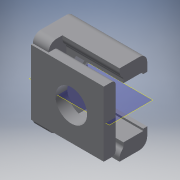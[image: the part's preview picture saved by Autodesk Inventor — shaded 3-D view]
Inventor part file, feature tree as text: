
AUTODESK INVENTOR PART (.ipt)
format: ipt  version: 2016 (Build 200138000, 138)  size: 312,320 bytes
history: native  units: mm
features: extrude x14, sketch x14, projected_geometry x7, fillet x3, plane x1, mirror x1, move_body x1
ambient origin geometry x8: Origin, YZ Plane, XZ Plane, XY Plane, X Axis, Y Axis, Z Axis, Center Point
bodies: Solid1 (feature_tree)
feature tree (41):
  extrude  "Extrusion1"  Depth=16.5mm
  sketch  "Sketch2"  dims[d2=11.0mm d3=0.0mm d4=6.0mm]
  extrude  "Extrusion2"  Depth=6.0mm
  extrude  "Extrusion3"  Depth=2.0mm
  extrude  "Extrusion4"  Depth=13.0mm
  extrude  "Extrusion5"  Depth=8.0mm
  extrude  "Extrusion6"  Depth=12.5mm TaperAngle=0.0deg
  extrude  "Extrusion7"  Depth=12.5mm TaperAngle=0.0deg
  extrude  "Extrusion8"  Depth=1.0mm TaperAngle=0.0deg
  extrude  "Extrusion9"  Depth=16.5mm
  extrude  "Extrusion10"  Depth=1.0mm
  plane  "Work Plane1"
  mirror  "Mirror1"
  extrude  "Extrusion11"  Depth=2.0mm TaperAngle=0.0deg
  fillet  "Fillet3"  Radius=2.0mm
  fillet  "Fillet4"  Radius=2.0mm
  fillet  "Fillet5"  Radius=2.0mm
  extrude  "Extrusion12"  Depth=2.0mm TaperAngle=0.0deg
  extrude  "Extrusion13"  Depth=0.5mm
  extrude  "Extrusion14"  Depth=2.0mm TaperAngle=0.0deg
  move_body  "Move Body1"
  sketch  "Sketch1"  dims[d0=16.5mm d1=16.5mm]
  projected_geometry  "Projected Loop1"
  sketch  "Sketch3"  dims[d5=1.0mm d6=2.0mm]
  sketch  "Sketch4"  dims[d7=1.0mm d8=13.0mm]
  sketch  "Sketch5"  dims[d9=5.0mm d10=0.0mm d11=8.0mm]
  sketch  "Sketch6"  dims[d12=20.0mm d13=0.0mm d14=12.5mm d15=0.0mm]
  projected_geometry  "Projected Loop2"
  sketch  "Sketch7"  dims[d16=13.0mm d17=12.5mm d18=0.0mm]
  projected_geometry  "Projected Loop3"
  sketch  "Sketch8"  dims[d19=2.0mm d20=0.0mm d21=1.0mm d22=0.0mm]
  projected_geometry  "Projected Loop4"
  sketch  "Sketch10"  dims[d24=3.0mm d25=0.0mm d28=16.5mm]
  sketch  "Sketch11"  dims[d29=2.0mm d30=1.0mm]
  sketch  "Sketch12"  dims[d31=2.0mm d32=0.0mm d33=2.0mm d34=0.0mm d36=2.0mm d37=0.0mm d38=2.0mm d39=2.0mm]
  sketch  "Sketch13"  dims[d40=2.0mm d41=3.0mm d42=0.0mm]
  projected_geometry  "Projected Loop7"
  sketch  "Sketch14"  dims[d43=2.0mm d44=0.0mm d45=0.5mm]
  projected_geometry  "Projected Loop8"
  sketch  "Sketch15"  dims[d46=1.0mm d47=0.0mm d48=0.0mm d49=2.0mm d50=0.0mm]
  projected_geometry  "Projected Loop9"
